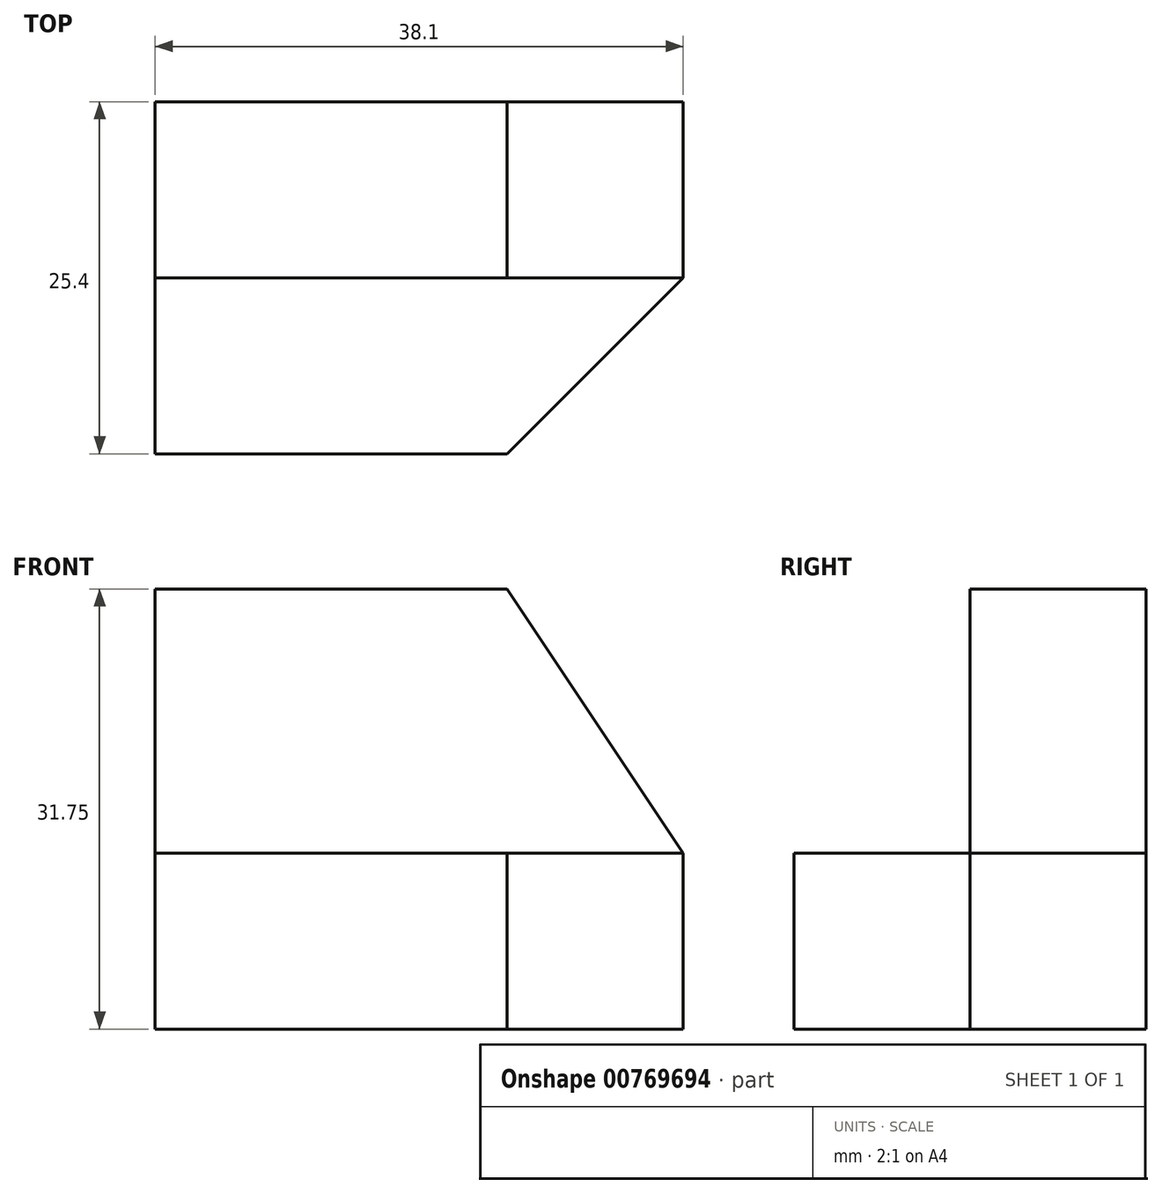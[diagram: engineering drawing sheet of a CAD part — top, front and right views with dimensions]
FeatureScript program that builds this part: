
annotation { "Feature Type Name" : "Feature", "Feature Type Description" : "" }
export const myFeature = defineFeature(function(context is Context, id is Id, definition is map)
    precondition{}
    {
        {
            var Q0;
            Q0=qCreatedBy(makeId("Front.planeOp"),FACE);
            var sketch = newSketch(context, id + "F0", { "sketchPlane" : qUnion([Q0])});
            skLineSegment(sketch, "E0", {"start": v(0, 0) * mm, "end": v(0, 31.75) * mm});
            skLineSegment(sketch, "E1", {"start": v(0, 31.75) * mm, "end": v(38.1, 31.75) * mm});
            skLineSegment(sketch, "E2", {"start": v(38.1, 31.75) * mm, "end": v(38.1, 0) * mm});
            skLineSegment(sketch, "E3", {"start": v(38.1, 0) * mm, "end": v(0, 0) * mm});
            skLineSegment(sketch, "E4", {"start": v(38.1, 0) * mm, "end": v(38.1, 6.35) * mm});
            skLineSegment(sketch, "E5", {"start": v(0, 31.75) * mm, "end": v(25.4, 31.75) * mm});
            skLineSegment(sketch, "E6", {"start": v(38.1, 6.35) * mm, "end": v(38.1, 12.7) * mm});
            skLineSegment(sketch, "E7", {"start": v(38.1, 12.7) * mm, "end": v(25.4, 31.75) * mm});
            skSolve(sketch);
        }
        {
            var Q0;
            Q0 = qSketchRegion(id + "F0", true);
            extrude(context, id + "F1", {"entities" : qUnion([Q0]), "depth" : 25.4 * mm, "offsetDistance" : 25.4 * mm});
        }
        {
            var Q0;
            Q0=makeQuery(id+"F1.opExtrude","SWEPT_FACE",FACE,{"disambiguationData":[OSD([sQuery(id+"F0.wireOp",EDGE,"E1"),sQuery(id+"F0.wireOp",EDGE,"E5")])]});
            var sketch = newSketch(context, id + "F2", { "sketchPlane" : qUnion([Q0])});
            skLineSegment(sketch, "E8", {"start": v(38.1, -25.4) * mm, "end": v(38.1, -12.7) * mm});
            skLineSegment(sketch, "E9", {"start": v(38.1, -12.7) * mm, "end": v(0, -12.7) * mm});
            skSolve(sketch);
        }
        {
            var Q0;
            Q0 = qSketchRegion(id + "F2", true);
            var Q1;
            Q1=makeQuery(id+"F2.imprint","IMPRINT",FACE,{"disambiguationData":[TD([[makeQuery(id+"F2.imprint","IMPRINT",EDGE,{"derivedFrom":sQuery(id+"F2.wireOp",EDGE,"E8")}),1.0]])]});
            extrude(context, id + "F3", {"entities" : qUnion([Q0, Q1]), "operationType" : NewBodyOperationType.REMOVE, "oppositeDirection" : true, "depth" : 19.05 * mm, "offsetDistance" : 25.4 * mm});
        }
        {
            var Q0;
            Q0=makeQuery(id+"F0.imprint","IMPRINT",FACE,{"disambiguationData":[TD([[makeQuery(id+"F0.imprint","IMPRINT",EDGE,{"derivedFrom":sQuery(id+"F0.wireOp",EDGE,"E1")}),-1.0]])]});
            extrude(context, id + "F4", {"entities" : qUnion([Q0]), "operationType" : NewBodyOperationType.REMOVE, "oppositeDirection" : true, "depth" : -12.7 * mm, "offsetDistance" : 25.4 * mm});
        }
        {
            var Q0;
            Q0=makeQuery(id+"F3.boolean.opBoolean","COPY",FACE,{"derivedFrom":makeQuery(id+"F3.opExtrude","CAP_FACE",FACE,{"disambiguationData":[OSD([sQuery(id+"F0.wireOp",EDGE,"E0"),sQuery(id+"F0.wireOp",EDGE,"E1"),sQuery(id+"F0.wireOp",EDGE,"E5"),sQuery(id+"F2.wireOp",EDGE,"E8"),sQuery(id+"F2.wireOp",EDGE,"E9")])],"isStart":false})});
            var sketch = newSketch(context, id + "F5", { "sketchPlane" : qUnion([Q0])});
            skLineSegment(sketch, "E10", {"start": v(38.1, -25.4) * mm, "end": v(25.4, -25.4) * mm});
            skLineSegment(sketch, "E11", {"start": v(25.4, -25.4) * mm, "end": v(38.1, -12.7) * mm});
            skSolve(sketch);
        }
        {
            var Q0;
            Q0 = qSketchRegion(id + "F5", true);
            var Q1;
            Q1=makeQuery(id+"F5.imprint","IMPRINT",FACE,{"disambiguationData":[TD([[makeQuery(id+"F5.imprint","IMPRINT",EDGE,{"derivedFrom":sQuery(id+"F5.wireOp",EDGE,"E10")}),1.0]])]});
            extrude(context, id + "F6", {"entities" : qUnion([Q0, Q1]), "operationType" : NewBodyOperationType.REMOVE, "oppositeDirection" : true, "depth" : 25.4 * mm, "offsetDistance" : 25.4 * mm});
        }
    });
